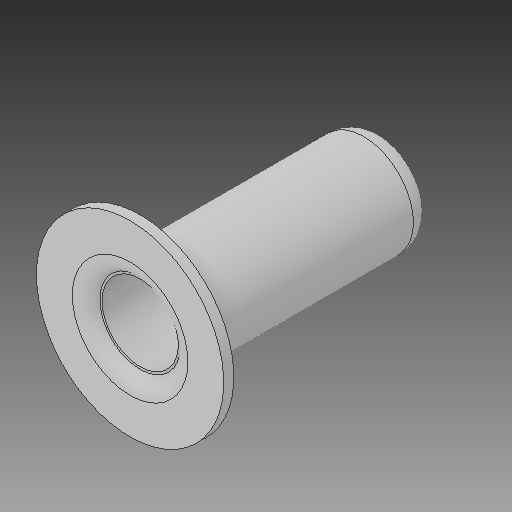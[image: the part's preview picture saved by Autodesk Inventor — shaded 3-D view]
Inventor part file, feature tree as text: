
AUTODESK INVENTOR PART (.ipt)
format: ipt  version: 2018 (Build 220112000, 112)  size: 127,488 bytes
history: native  units: in
note: dims shown in document units (in); Inventor stores cm internally (conversion verified against a paired STEP export)
features: fillet x1
ambient origin geometry x8: Origin, YZ Plane, XZ Plane, XY Plane, X Axis, Y Axis, Z Axis, Center Point
bodies: Solid1 (feature_tree)
feature tree (1):
  fillet  "Fillet1"  [1 undecoded]
note: 1 required parameter value undecoded (feature->parameter linkage not recoverable at this tier; creation-order binding heuristic only, values carry confidence <= 0.55)
